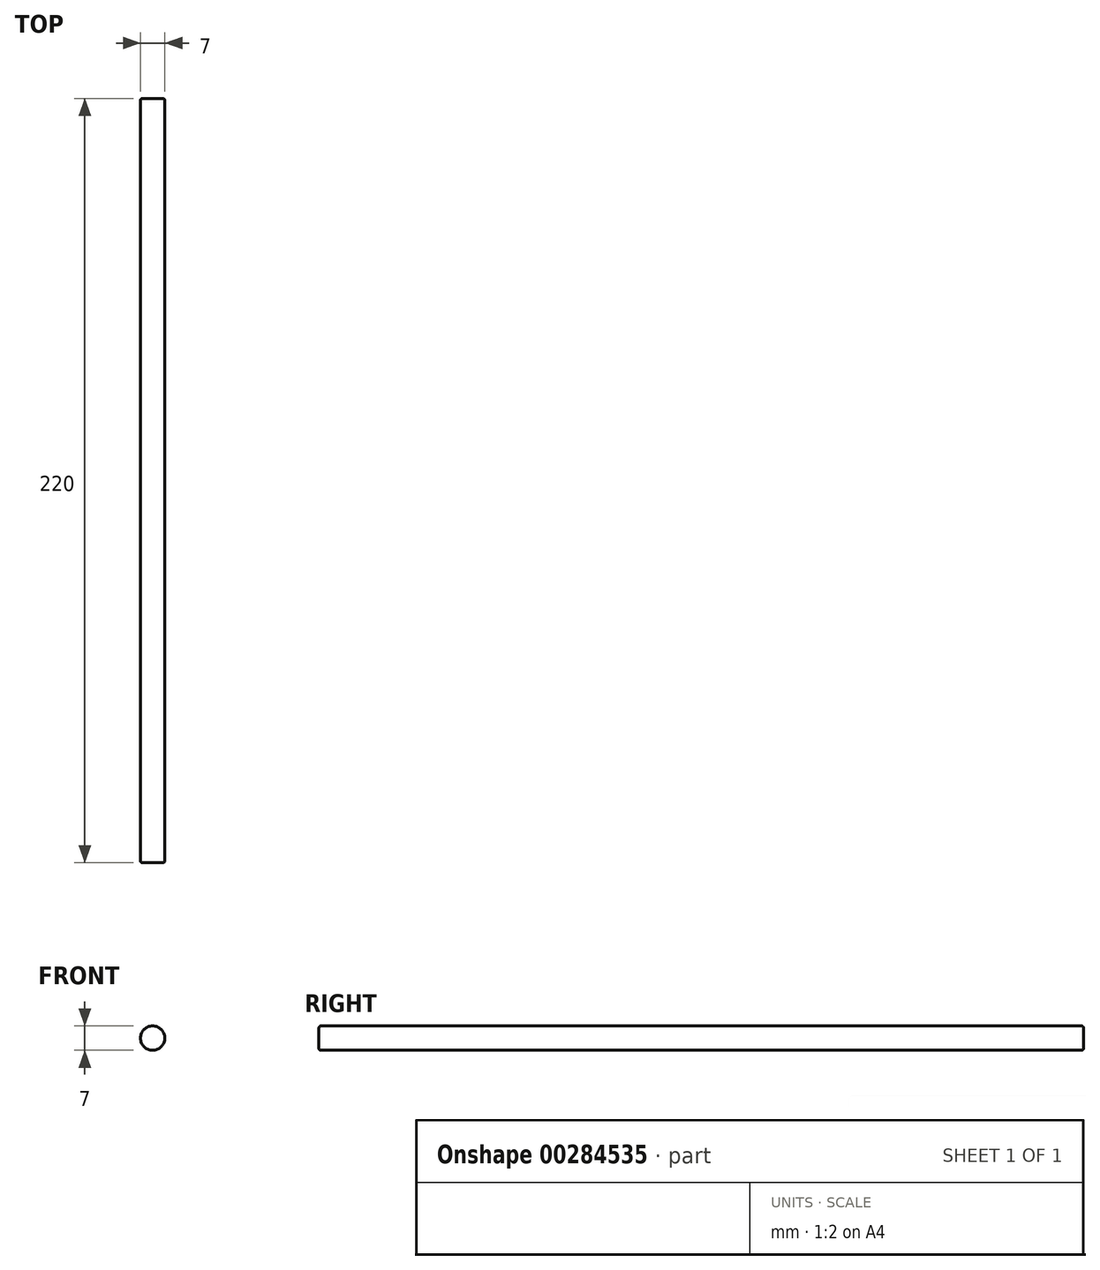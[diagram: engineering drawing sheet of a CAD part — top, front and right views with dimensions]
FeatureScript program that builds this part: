
annotation { "Feature Type Name" : "Feature", "Feature Type Description" : "" }
export const myFeature = defineFeature(function(context is Context, id is Id, definition is map)
    precondition{}
    {
        {
            var Q0;
            Q0=qCreatedBy(makeId("Front.planeOp"),FACE);
            var sketch = newSketch(context, id + "F0", { "sketchPlane" : qUnion([Q0])});
            skCircle(sketch, "E0", {"center": v(0, 0) * mm, "radius": 3.5 * mm});
            skSolve(sketch);
        }
        {
            var Q0;
            Q0=qSketchRegion(id+"F0",true);
            extrude(context, id + "F1", {"entities" : qUnion([Q0]), "endBound" : BoundingType.SYMMETRIC, "depth" : 220 * mm});
        }
        {
            var Q0;
            Q0=makeQuery(id+"F1.opExtrude","CAP_EDGE",EDGE,{"disambiguationData":[OSD([sQuery(id+"F0.wireOp",EDGE,"E0")])],"isStart":false});
            var Q1;
            Q1=makeQuery(id+"F1.opExtrude","CAP_EDGE",EDGE,{"disambiguationData":[OSD([sQuery(id+"F0.wireOp",EDGE,"E0")])],"isStart":true});
            fillet(context, id + "F2", {"entities" : qUnion([Q0, Q1]), "radius" : 0.5 * mm, "tangentPropagation" : true, "allowEdgeOverflow" : false});
        }
    });
